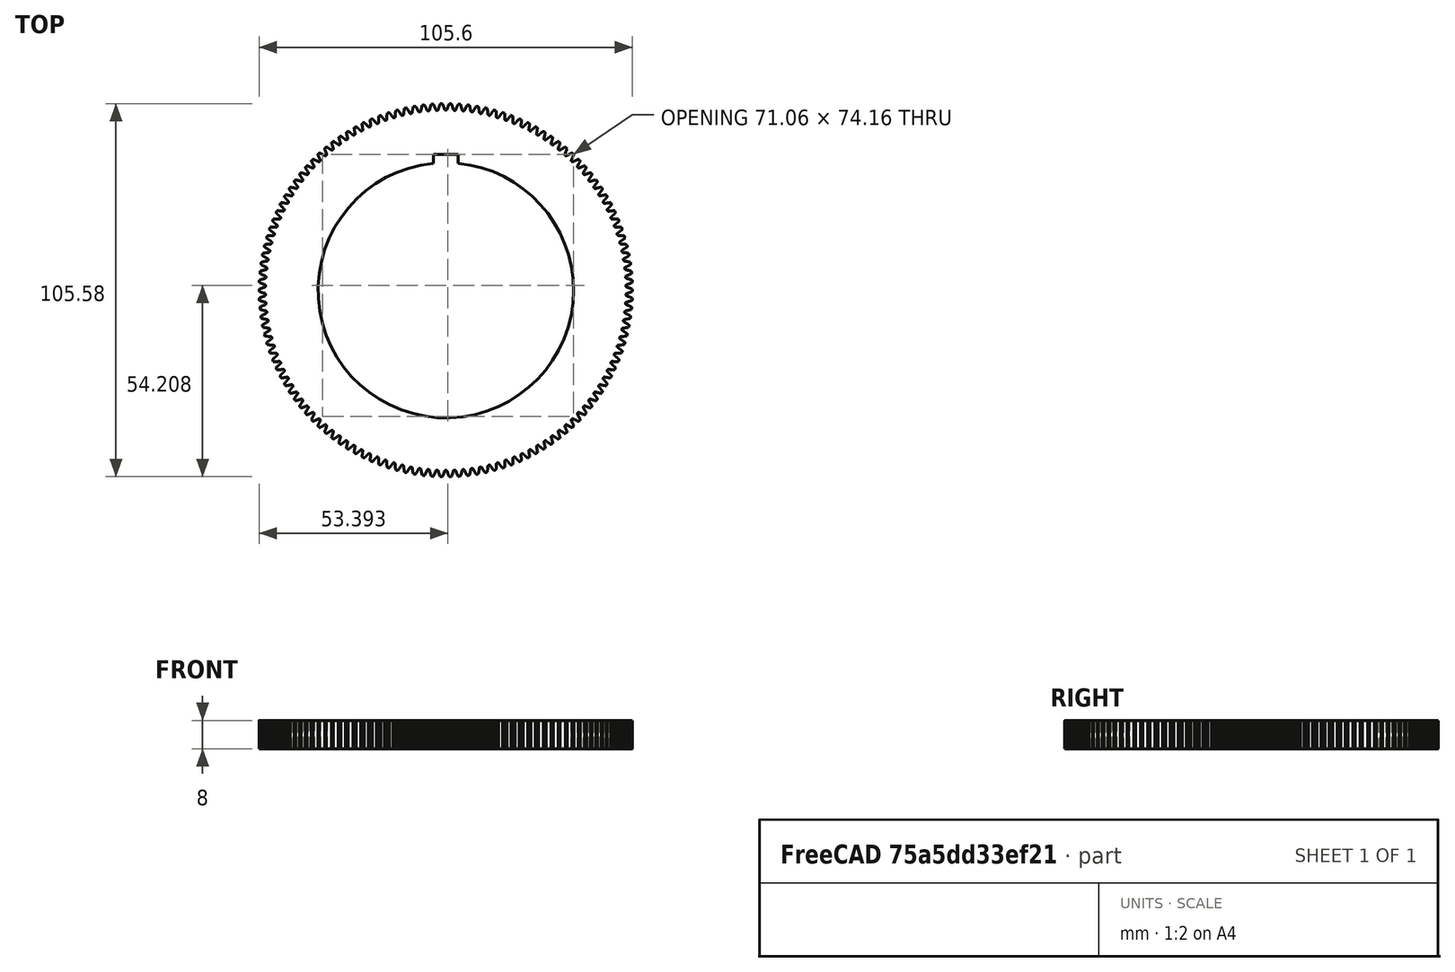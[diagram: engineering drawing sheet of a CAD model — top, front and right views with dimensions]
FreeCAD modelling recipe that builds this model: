
FCSTD DOCUMENT  (FreeCAD 0.15R4671 (Git))
Label: foton-37-140-ff-notch
License: Creative Commons - Attribution - Share Alike license
LicenseURL: http://creativecommons.org/licenses/by-sa/3.0/
objects: Part::Cut×2, Part::Part2DObjectPython×1, PartDesign::Pad×1, Sketcher::SketchObject×1, PartDesign::Pocket×1, Part::Box×1
note: 9 computed .brp shape members not serialized (recipe doc carries the construction recipe); baked Part::Feature solids carry a one-line shape summary decoded from their .brp

FEATURE [Part::Part2DObjectPython] InvoluteGear  # Draft 2D object (typed FeaturePython)
  ExternalGear = true
  HighPrecision = true
  Modules = 0.8
  NumberOfTeeth = 130
  PressureAngle = 20
FEATURE [PartDesign::Pad] Pad001  label="Gear"
  Length = 8
  Length2 = 100
  Sketch = -> InvoluteGear
  Type = 0
FEATURE [Sketcher::SketchObject] Sketch
  Placement = pos=(0,0,8) rot=(0,0,1;0rad)
  Support = -> Pad001 [Face1042]
  sketch-geometry (1):
    g0: Circle CenterX=0 CenterY=0 CenterZ=0 NormalX=0 NormalY=0 NormalZ=1 Radius=36.125
  constraints (1):
    c: Radius(g0) = 36.125
FEATURE [PartDesign::Pocket] Pocket001  label="Focus Gear"
  Length = 15
  Sketch = -> Sketch
  Type = 0
FEATURE [Part::Box] Box  label="Notch"
  Height = 10
  Length = 7
  Placement = pos=(-3.5,34,-1) rot=(0,0,1;0rad)
  Width = 4.5
FEATURE [Part::Cut] Cut
  Base = -> Pocket001
  Tool = -> Box
FEATURE [Part::Cut] Cut001  label="Notched"
  Base = -> Pocket001
  Tool = -> Box
